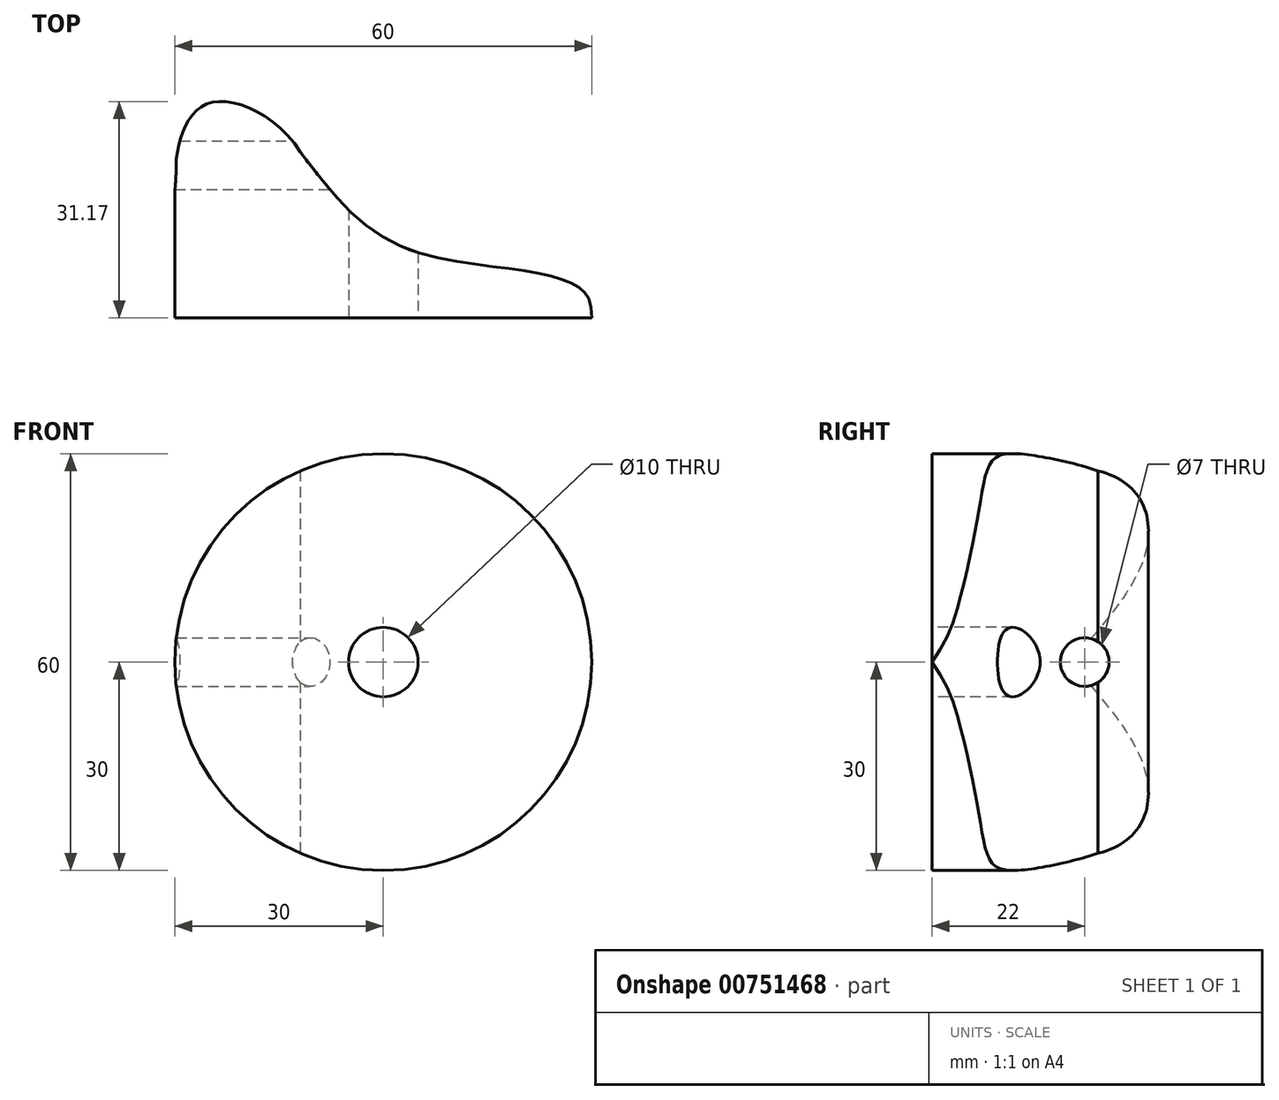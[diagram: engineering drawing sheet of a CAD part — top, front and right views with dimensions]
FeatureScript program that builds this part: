
annotation { "Feature Type Name" : "Feature", "Feature Type Description" : "" }
export const myFeature = defineFeature(function(context is Context, id is Id, definition is map)
    precondition{}
    {
        {
            var Q0;
            Q0=qCreatedBy(makeId("Front.planeOp"),FACE);
            var sketch = newSketch(context, id + "F0", { "sketchPlane" : qUnion([Q0])});
            skCircle(sketch, "E0", {"center": v(0, 0) * mm, "radius": 30 * mm});
            skSolve(sketch);
        }
        {
            var Q0;
            Q0=qCreatedBy(makeId("Top.planeOp"),FACE);
            var sketch = newSketch(context, id + "F1", { "sketchPlane" : qUnion([Q0])});
            skLineSegment(sketch, "E1", {"start": v(-30, 0) * mm, "end": v(-30, 20) * mm});
            skFitSpline(sketch, "E2", {"points": [v(-11.97, 23.92) * mm, v(2.03, 10.55) * mm, v(22.1, 6.5) * mm, v(29.22, 3.38) * mm, v(30, 0) * mm], "startDerivative": vector(39.57, -51.21) * mm, "endDerivative": vector(0.84, -28.72) * mm});
            skFitSpline(sketch, "E3", {"points": [v(-30, 20) * mm, v(-25.24, 30.87) * mm, v(-11.97, 23.92) * mm], "startDerivative": vector(0, 27.55) * mm, "endDerivative": vector(15.24, -26.33) * mm});
            skLineSegment(sketch, "E4", {"start": v(-30, 0) * mm, "end": v(30, 0) * mm});
            skSolve(sketch);
        }
        {
            var Q0;
            Q0=makeQuery(id+"F1.imprint","IMPRINT",FACE,{"disambiguationData":[TD([[makeQuery(id+"F1.imprint","IMPRINT",EDGE,{"derivedFrom":sQuery(id+"F1.wireOp",EDGE,"E1")}),-1.0]])]});
            extrude(context, id + "F2", {"entities" : qUnion([Q0]), "endBound" : BoundingType.SYMMETRIC, "depth" : 60 * mm, "offsetDistance" : 25 * mm});
        }
        {
            var Q0;
            Q0=makeQuery(id+"F0.imprint","IMPRINT",FACE,{"disambiguationData":[TD([[makeQuery(id+"F0.imprint","IMPRINT",EDGE,{"derivedFrom":sQuery(id+"F0.wireOp",EDGE,"E0")}),1.0]])]});
            extrude(context, id + "F3", {"entities" : qUnion([Q0]), "operationType" : NewBodyOperationType.INTERSECT, "oppositeDirection" : true, "depth" : 42.6 * mm, "offsetDistance" : 25 * mm});
        }
        {
            var Q0;
            Q0=qCreatedBy(makeId("Front.planeOp"),FACE);
            var sketch = newSketch(context, id + "F4", { "sketchPlane" : qUnion([Q0])});
            skCircle(sketch, "E5", {"center": v(0, 0) * mm, "radius": 5 * mm});
            skSolve(sketch);
        }
        {
            var Q0;
            Q0 = qSketchRegion(id + "F4", true);
            extrude(context, id + "F5", {"entities" : qUnion([Q0]), "operationType" : NewBodyOperationType.REMOVE, "oppositeDirection" : true, "depth" : 25 * mm, "offsetDistance" : 25 * mm});
        }
        {
            var Q0;
            Q0=qCreatedBy(makeId("Right.planeOp"),FACE);
            var sketch = newSketch(context, id + "F6", { "sketchPlane" : qUnion([Q0])});
            skCircle(sketch, "E6", {"center": v(22, 0) * mm, "radius": 3.5 * mm});
            skSolve(sketch);
        }
        {
            var Q0;
            Q0 = qSketchRegion(id + "F6", true);
            extrude(context, id + "F7", {"entities" : qUnion([Q0]), "operationType" : NewBodyOperationType.REMOVE, "oppositeDirection" : true, "depth" : 30 * mm, "offsetDistance" : 25 * mm});
        }
    });
